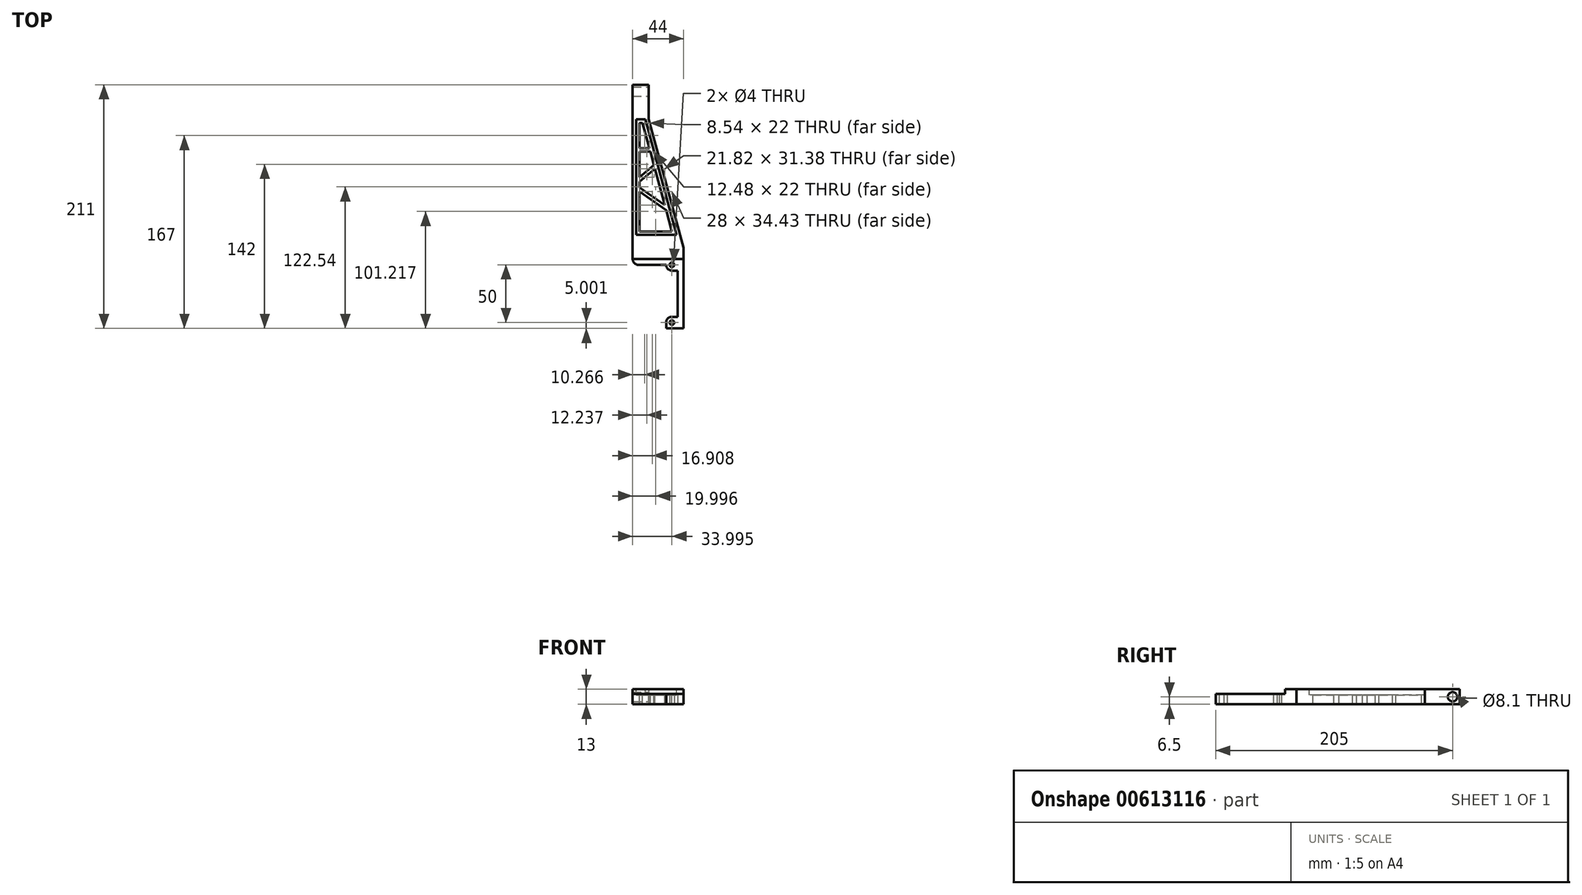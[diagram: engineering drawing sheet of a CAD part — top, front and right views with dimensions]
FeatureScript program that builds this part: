
annotation { "Feature Type Name" : "Feature", "Feature Type Description" : "" }
export const myFeature = defineFeature(function(context is Context, id is Id, definition is map)
    precondition{}
    {
        {
            var Q0;
            Q0=qCreatedBy(makeId("Top.planeOp"),FACE);
            var sketch = newSketch(context, id + "F0", { "sketchPlane" : qUnion([Q0])});
            skLineSegment(sketch, "E0", {"start": v(-21.22, 91.37) * mm, "end": v(-21.22, 61.37) * mm});
            skLineSegment(sketch, "E1", {"start": v(-21.22, 61.37) * mm, "end": v(8.78, -49.63) * mm});
            skLineSegment(sketch, "E2", {"start": v(8.78, -49.63) * mm, "end": v(8.78, -119.63) * mm});
            skLineSegment(sketch, "E3", {"start": v(8.78, -119.63) * mm, "end": v(-6.22, -119.63) * mm});
            skLineSegment(sketch, "E4", {"start": v(-6.22, -119.63) * mm, "end": v(-6.22, -109.63) * mm});
            skLineSegment(sketch, "E5", {"start": v(-6.22, -109.63) * mm, "end": v(3.78, -109.63) * mm});
            skLineSegment(sketch, "E6", {"start": v(3.78, -109.63) * mm, "end": v(3.78, -69.63) * mm});
            skLineSegment(sketch, "E7", {"start": v(3.78, -69.63) * mm, "end": v(-6.22, -69.63) * mm});
            skLineSegment(sketch, "E8", {"start": v(-6.22, -69.63) * mm, "end": v(-6.22, -64.63) * mm});
            skLineSegment(sketch, "E9", {"start": v(-6.22, -64.63) * mm, "end": v(-35.22, -64.63) * mm});
            skLineSegment(sketch, "E10", {"start": v(-35.22, -64.63) * mm, "end": v(-35.22, 91.37) * mm});
            skPoint(sketch, "E11", {"position": v(-35.22, 91.37) * mm});
            skLineSegment(sketch, "E12", {"start": v(-35.22, 91.37) * mm, "end": v(-21.22, 91.37) * mm});
            skLineSegment(sketch, "E13", {"start": v(8.78, -59.63) * mm, "end": v(-35.22, -59.63) * mm});
            skCircle(sketch, "E14", {"center": v(-1.22, -64.63) * mm, "radius": 2 * mm});
            skCircle(sketch, "E15", {"center": v(-1.22, -114.63) * mm, "radius": 2 * mm});
            skPoint(sketch, "E16", {"position": v(-1.22, -109.63) * mm});
            skSolve(sketch);
        }
        {
            var Q0;
            {var subQ3=sQuery(id+"F0.wireOp",EDGE,"E3");Q0=makeQuery(id+"F0.imprint","IMPRINT",FACE,{"disambiguationData":[TD([[makeQuery(id+"F0.imprint","IMPRINT",EDGE,{"derivedFrom":subQ3}),-1.0]])]});}
            extrude(context, id + "F1", {"entities" : qUnion([Q0]), "depth" : 9 * mm, "offsetDistance" : 25 * mm});
        }
        {
            var Q0;
            Q0=makeQuery(id+"F0.imprint","IMPRINT",FACE,{"disambiguationData":[TD([[makeQuery(id+"F0.imprint","IMPRINT",EDGE,{"derivedFrom":sQuery(id+"F0.wireOp",EDGE,"E0")}),-1.0]])]});
            extrude(context, id + "F2", {"entities" : qUnion([Q0]), "operationType" : NewBodyOperationType.ADD, "depth" : 13 * mm, "offsetDistance" : 25 * mm});
        }
        {
            var Q0;
            Q0=makeQuery(id+"F2.opExtrude","CAP_FACE",FACE,{"disambiguationData":[OSD([sQuery(id+"F0.wireOp",EDGE,"E0"),sQuery(id+"F0.wireOp",EDGE,"E1"),sQuery(id+"F0.wireOp",EDGE,"E2"),sQuery(id+"F0.wireOp",EDGE,"E10"),sQuery(id+"F0.wireOp",EDGE,"E12"),sQuery(id+"F0.wireOp",EDGE,"E13")])],"isStart":false});
            var sketch = newSketch(context, id + "F3", { "sketchPlane" : qUnion([Q0])});
            skLineSegment(sketch, "E17", {"start": v(-24.33, 61.37) * mm, "end": v(2.7, -38.63) * mm});
            skLineSegment(sketch, "E18", {"start": v(2.7, -38.63) * mm, "end": v(-32.22, -38.63) * mm});
            skLineSegment(sketch, "E19", {"start": v(-32.22, -38.63) * mm, "end": v(-32.22, 61.37) * mm});
            skLineSegment(sketch, "E20", {"start": v(-32.22, 61.37) * mm, "end": v(-24.33, 61.37) * mm});
            skSolve(sketch);
        }
        {
            var Q0;
            Q0=makeQuery(id+"F3.imprint","IMPRINT",FACE,{"disambiguationData":[TD([[makeQuery(id+"F3.imprint","IMPRINT",EDGE,{"derivedFrom":sQuery(id+"F3.wireOp",EDGE,"E17")}),-1.0]])]});
            extrude(context, id + "F4", {"entities" : qUnion([Q0]), "operationType" : NewBodyOperationType.REMOVE, "oppositeDirection" : true, "depth" : 5 * mm, "offsetDistance" : 25 * mm});
        }
        {
            var Q0;
            Q0=makeQuery(id+"F4.boolean.opBoolean","COPY",FACE,{"derivedFrom":makeQuery(id+"F4.opExtrude","CAP_FACE",FACE,{"disambiguationData":[OSD([sQuery(id+"F3.wireOp",EDGE,"E17"),sQuery(id+"F3.wireOp",EDGE,"E18"),sQuery(id+"F3.wireOp",EDGE,"E19"),sQuery(id+"F3.wireOp",EDGE,"E20")])],"isStart":false})});
            var sketch = newSketch(context, id + "F5", { "sketchPlane" : qUnion([Q0])});
            skLineSegment(sketch, "E21", {"start": v(-29.22, 58.37) * mm, "end": v(-29.22, -35.63) * mm});
            skLineSegment(sketch, "E22", {"start": v(-29.22, -35.63) * mm, "end": v(-1.22, -35.63) * mm});
            skLineSegment(sketch, "E23", {"start": v(-1.22, -35.63) * mm, "end": v(-26.63, 58.37) * mm});
            skLineSegment(sketch, "E24", {"start": v(-26.63, 58.37) * mm, "end": v(-29.22, 58.37) * mm});
            skLineSegment(sketch, "E25", {"start": v(-29.22, 36.37) * mm, "end": v(-29.22, 36.37) * mm});
            skLineSegment(sketch, "E26", {"start": v(-29.22, 33.37) * mm, "end": v(-29.22, 33.37) * mm});
            skLineSegment(sketch, "E27", {"start": v(-29.22, 11.37) * mm, "end": v(-16.74, 21.79) * mm});
            skLineSegment(sketch, "E28", {"start": v(-29.22, 7.46) * mm, "end": v(-15.88, 18.6) * mm});
            skLineSegment(sketch, "E29", {"start": v(-29.22, 2.46) * mm, "end": v(-7.4, -12.78) * mm});
            skLineSegment(sketch, "E30", {"start": v(-29.22, -1.2) * mm, "end": v(-6.18, -17.29) * mm});
            skLineSegment(sketch, "E31", {"start": v(-29.22, 36.37) * mm, "end": v(-20.68, 36.37) * mm});
            skLineSegment(sketch, "E32", {"start": v(-29.22, 33.37) * mm, "end": v(-19.87, 33.37) * mm});
            skSolve(sketch);
        }
        {
            var Q0;
            {var subQ0=sQuery(id+"F5.wireOp",EDGE,"E24");Q0=makeQuery(id+"F5.imprint","IMPRINT",FACE,{"disambiguationData":[TD([[makeQuery(id+"F5.imprint","IMPRINT",EDGE,{"derivedFrom":subQ0}),1.0]])]});}
            var Q1;
            {var subQ0=sQuery(id+"F5.wireOp",EDGE,"E27");Q1=makeQuery(id+"F5.imprint","IMPRINT",FACE,{"disambiguationData":[TD([[makeQuery(id+"F5.imprint","IMPRINT",EDGE,{"derivedFrom":subQ0}),1.0]])]});}
            var Q2;
            {var subQ0=sQuery(id+"F5.wireOp",EDGE,"E28");Q2=makeQuery(id+"F5.imprint","IMPRINT",FACE,{"disambiguationData":[TD([[makeQuery(id+"F5.imprint","IMPRINT",EDGE,{"derivedFrom":subQ0}),-1.0]])]});}
            var Q3;
            {var subQ0=sQuery(id+"F5.wireOp",EDGE,"E22");Q3=makeQuery(id+"F5.imprint","IMPRINT",FACE,{"disambiguationData":[TD([[makeQuery(id+"F5.imprint","IMPRINT",EDGE,{"derivedFrom":subQ0}),1.0]])]});}
            extrude(context, id + "F6", {"entities" : qUnion([Q0, Q1, Q2, Q3]), "operationType" : NewBodyOperationType.REMOVE, "endBound" : BoundingType.THROUGH_ALL, "oppositeDirection" : true, "depth" : 25 * mm, "offsetDistance" : 25 * mm});
        }
        {
            var Q0;
            Q0=makeQuery(id+"F1.opExtrude","SWEPT_EDGE",EDGE,{"disambiguationData":[OSD([sQuery(id+"F0.wireOp",EDGE,"E7"),sQuery(id+"F0.wireOp",EDGE,"E8")])]});
            fillet(context, id + "F7", {"entities" : qUnion([Q0]), "radius" : 5 * mm, "tangentPropagation" : true, "allowEdgeOverflow" : false});
        }
        {
            var Q0;
            Q0=makeQuery(id+"F1.opExtrude","SWEPT_EDGE",EDGE,{"disambiguationData":[OSD([sQuery(id+"F0.wireOp",EDGE,"E4"),sQuery(id+"F0.wireOp",EDGE,"E5")])]});
            fillet(context, id + "F8", {"entities" : qUnion([Q0]), "radius" : 5 * mm, "tangentPropagation" : true, "allowEdgeOverflow" : false});
        }
        {
            var Q0;
            Q0=makeQuery(id+"F1.opExtrude","SWEPT_EDGE",EDGE,{"disambiguationData":[OSD([sQuery(id+"F0.wireOp",EDGE,"E9"),sQuery(id+"F0.wireOp",EDGE,"E10")])]});
            fillet(context, id + "F9", {"entities" : qUnion([Q0]), "radius" : 5 * mm, "tangentPropagation" : true, "allowEdgeOverflow" : false});
        }
        {
            var Q0;
            Q0=makeQuery(id+"F2.opExtrude","SWEPT_FACE",FACE,{"disambiguationData":[OSD([sQuery(id+"F0.wireOp",EDGE,"E0")])]});
            var sketch = newSketch(context, id + "F10", { "sketchPlane" : qUnion([Q0])});
            skCircle(sketch, "E33", {"center": v(85.37, 6.5) * mm, "radius": 4.05 * mm});
            skSolve(sketch);
        }
        {
            var Q0;
            Q0=makeQuery(id+"F10.imprint","IMPRINT",FACE,{"disambiguationData":[TD([[makeQuery(id+"F10.imprint","IMPRINT",EDGE,{"derivedFrom":sQuery(id+"F10.wireOp",EDGE,"E33")}),1.0]])]});
            extrude(context, id + "F11", {"entities" : qUnion([Q0]), "operationType" : NewBodyOperationType.REMOVE, "endBound" : BoundingType.THROUGH_ALL, "oppositeDirection" : true, "depth" : 25 * mm, "offsetDistance" : 25 * mm});
        }
    });
